# Revit family: VENTS-VK
name_source: partatom
category: Mechanical Equipment
units: mm (PartAtom-declared; Revit-internal decimal feet)

## family parameters
Always vertical = No
Classification = None
Cut with Voids When Loaded = No
OmniClass Number = 23.75.35.17.11
OmniClass Title = Fans for Air Ductwork
Part Type = Breaks Into
Room Calculation Point = No
Round Connector Dimension = Use Diameter
Shared = No
Work Plane-Based = No

## types (27) — shared parameters
Description = Inline centrifugal fan for round ducts
Family Version = 1.0
Fan Material = Plastic White Glazed
Load Classification = HVAC
Maintenance Zone Height = 600 mm
Maintenance Zone Length = 600 mm
Maintenance Zone Material = Maintenance Zone
Maintenance Zone Width = 600 mm
Manufacturer = Vents
Number of Poles = 1
Power Factor = 1
Protection rating = IPX4
R11 = 5 mm  [stored 0.0164042 ft]
R12 = 15 mm  [stored 0.0492126 ft]
R21 = 5 mm  [stored 0.0164042 ft]
R22 = 15 mm  [stored 0.0492126 ft]
URL = https://ventilation-system.com
Voltage = 230 V

## per-type parameters (varying)
- VK 100 (50Hz): Apparent Power=80 VA; BoxA=85 mm  [stored 0.278871 ft]; BoxAngle=90.00°; BoxD=250 mm  [stored 0.82021 ft]; BoxDepth=78 mm  [stored 0.255906 ft]; Current=0 A; D=100 mm  [stored 0.328084 ft]; D1=250 mm  [stored 0.82021 ft]; Duct Connection Size=100 mm  [stored 0.328084 ft]; L=230 mm  [stored 0.754593 ft]; L1=28 mm  [stored 0.0918635 ft]; L12=40 mm  [stored 0.131234 ft]; L13=40 mm  [stored 0.131234 ft]; L2=32 mm  [stored 0.104987 ft]; L22=70 mm; L23=20 mm  [stored 0.0656168 ft]; Maximum Air Flow=250 m³/h; Model=VK 100; Noise Level at 3 m (dBa)=40; Power=80 W; R1=125 mm  [stored 0.410105 ft]; RPM (min-1)=2820; Transported Air Temperature (°C)=-25...+60; Type Comments=Inline centrifugal fan VK 100; Weight=2.01 kg
- VK 100 (60Hz): Apparent Power=81 VA; BoxA=85 mm  [stored 0.278871 ft]; BoxAngle=90.00°; BoxD=250 mm  [stored 0.82021 ft]; BoxDepth=78 mm  [stored 0.255906 ft]; Current=0 A; D=100 mm  [stored 0.328084 ft]; D1=250 mm  [stored 0.82021 ft]; Duct Connection Size=100 mm  [stored 0.328084 ft]; L=230 mm  [stored 0.754593 ft]; L1=28 mm  [stored 0.0918635 ft]; L12=40 mm  [stored 0.131234 ft]; L13=40 mm  [stored 0.131234 ft]; L2=32 mm  [stored 0.104987 ft]; L22=70 mm; L23=20 mm  [stored 0.0656168 ft]; Maximum Air Flow=290 m³/h; Model=VK 100; Noise Level at 3 m (dBa)=41; Power=81 W; R1=125 mm  [stored 0.410105 ft]; RPM (min-1)=2890; Transported Air Temperature (°C)=-25...+40; Type Comments=Inline centrifugal fan VK 100; Weight=2.01 kg
- VK 125 (50Hz): Apparent Power=79 VA; BoxA=85 mm  [stored 0.278871 ft]; BoxAngle=90.00°; BoxD=250 mm  [stored 0.82021 ft]; BoxDepth=78 mm  [stored 0.255906 ft]; Current=0 A; D=125 mm  [stored 0.410105 ft]; D1=250 mm  [stored 0.82021 ft]; Duct Connection Size=125 mm  [stored 0.410105 ft]; L=220 mm  [stored 0.721785 ft]; L1=27 mm  [stored 0.0885827 ft]; L12=40 mm  [stored 0.131234 ft]; L13=40 mm  [stored 0.131234 ft]; L2=30 mm  [stored 0.0984252 ft]; L22=63 mm; L23=20 mm  [stored 0.0656168 ft]; Maximum Air Flow=355 m³/h; Model=VK 125; Noise Level at 3 m (dBa)=40; Power=79 W; R1=125 mm  [stored 0.410105 ft]; RPM (min-1)=2800; Transported Air Temperature (°C)=-25...+60; Type Comments=Inline centrifugal fan VK 125; Weight=2.20 kg
- VK 125 (60Hz): Apparent Power=81 VA; BoxA=85 mm  [stored 0.278871 ft]; BoxAngle=90.00°; BoxD=250 mm  [stored 0.82021 ft]; BoxDepth=78 mm  [stored 0.255906 ft]; Current=0 A; D=125 mm  [stored 0.410105 ft]; D1=250 mm  [stored 0.82021 ft]; Duct Connection Size=125 mm  [stored 0.410105 ft]; L=220 mm  [stored 0.721785 ft]; L1=27 mm  [stored 0.0885827 ft]; L12=40 mm  [stored 0.131234 ft]; L13=40 mm  [stored 0.131234 ft]; L2=30 mm  [stored 0.0984252 ft]; L22=63 mm; L23=20 mm  [stored 0.0656168 ft]; Maximum Air Flow=370 m³/h; Model=VK 125; Noise Level at 3 m (dBa)=41; Power=81 W; R1=125 mm  [stored 0.410105 ft]; RPM (min-1)=2830; Transported Air Temperature (°C)=-25...+40; Type Comments=Inline centrifugal fan VK 125; Weight=2.20 kg
- VK 150 (50Hz): Apparent Power=80 VA; BoxA=85 mm  [stored 0.278871 ft]; BoxAngle=90.00°; BoxD=300 mm; BoxDepth=86 mm  [stored 0.282152 ft]; Current=0 A; D=150 mm; D1=300 mm; Duct Connection Size=150 mm; L=286 mm; L1=56 mm  [stored 0.183727 ft]; L12=17 mm; L13=48 mm  [stored 0.15748 ft]; L2=64 mm  [stored 0.209974 ft]; L22=71 mm; L23=30 mm  [stored 0.0984252 ft]; Maximum Air Flow=460 m³/h; Model=VK 150; Noise Level at 3 m (dBa)=42; Power=80 W; R1=150 mm; RPM (min-1)=2725; Transported Air Temperature (°C)=-25...+60; Type Comments=Inline centrifugal fan VK 150; Weight=2.45 kg
- VK 150 (60Hz): Apparent Power=84 VA; BoxA=85 mm  [stored 0.278871 ft]; BoxAngle=90.00°; BoxD=300 mm; BoxDepth=86 mm  [stored 0.282152 ft]; Current=0 A; D=150 mm; D1=300 mm; Duct Connection Size=150 mm; L=286 mm; L1=56 mm  [stored 0.183727 ft]; L12=17 mm; L13=48 mm  [stored 0.15748 ft]; L2=64 mm  [stored 0.209974 ft]; L22=71 mm; L23=30 mm  [stored 0.0984252 ft]; Maximum Air Flow=505 m³/h; Model=VK 150; Noise Level at 3 m (dBa)=43; Power=84 W; R1=150 mm; RPM (min-1)=2840; Transported Air Temperature (°C)=-25...+40; Type Comments=Inline centrifugal fan VK 150; Weight=2.45 kg
- VK 200 (50Hz): Apparent Power=107 VA; BoxA=120 mm  [stored 0.393701 ft]; BoxAngle=60.00°; BoxD=340 mm; BoxDepth=83 mm  [stored 0.27231 ft]; Current=0 A; D=200 mm  [stored 0.656168 ft]; D1=340 mm; Duct Connection Size=200 mm  [stored 0.656168 ft]; L=276 mm  [stored 0.905512 ft]; L1=28 mm  [stored 0.0918635 ft]; L12=26 mm; L13=68 mm; L2=28 mm  [stored 0.0918635 ft]; L22=98 mm; L23=28 mm  [stored 0.0918635 ft]; Maximum Air Flow=780 m³/h; Model=VK 200; Noise Level at 3 m (dBa)=46; Power=107 W; R1=170 mm  [stored 0.557743 ft]; RPM (min-1)=2660; Transported Air Temperature (°C)=-25...+60; Type Comments=Inline centrifugal fan VK 200; Weight=3.00 kg
- VK 200 (60Hz): Apparent Power=132 VA; BoxA=120 mm  [stored 0.393701 ft]; BoxAngle=60.00°; BoxD=340 mm; BoxDepth=83 mm  [stored 0.27231 ft]; Current=1 A; D=200 mm  [stored 0.656168 ft]; D1=340 mm; Duct Connection Size=200 mm  [stored 0.656168 ft]; L=276 mm  [stored 0.905512 ft]; L1=28 mm  [stored 0.0918635 ft]; L12=26 mm; L13=68 mm; L2=28 mm  [stored 0.0918635 ft]; L22=98 mm; L23=28 mm  [stored 0.0918635 ft]; Maximum Air Flow=890 m³/h; Model=VK 200; Noise Level at 3 m (dBa)=46; Power=132 W; R1=170 mm  [stored 0.557743 ft]; RPM (min-1)=2765; Transported Air Temperature (°C)=-25...+40; Type Comments=Inline centrifugal fan VK 200; Weight=3.00 kg
- VKS 200 (50Hz): Apparent Power=173 VA; BoxA=120 mm  [stored 0.393701 ft]; BoxAngle=60.00°; BoxD=366 mm; BoxDepth=83 mm  [stored 0.27231 ft]; Current=1 A; D=200 mm  [stored 0.656168 ft]; D1=340 mm; Duct Connection Size=200 mm  [stored 0.656168 ft]; L=276 mm  [stored 0.905512 ft]; L1=28 mm  [stored 0.0918635 ft]; L12=26 mm; L13=68 mm; L2=28 mm  [stored 0.0918635 ft]; L22=98 mm; L23=28 mm  [stored 0.0918635 ft]; Maximum Air Flow=930 m³/h; Model=VKS 200; Noise Level at 3 m (dBa)=48; Power=173 W; R1=170 mm  [stored 0.557743 ft]; RPM (min-1)=2425; Transported Air Temperature (°C)=-25...+60; Type Comments=Inline centrifugal fan VKS 200; Weight=4.30 kg
- VKS 200 (60Hz): Apparent Power=216 VA; BoxA=120 mm  [stored 0.393701 ft]; BoxAngle=60.00°; BoxD=366 mm; BoxDepth=83 mm  [stored 0.27231 ft]; Current=1 A; D=200 mm  [stored 0.656168 ft]; D1=340 mm; Duct Connection Size=200 mm  [stored 0.656168 ft]; L=276 mm  [stored 0.905512 ft]; L1=28 mm  [stored 0.0918635 ft]; L12=26 mm; L13=68 mm; L2=28 mm  [stored 0.0918635 ft]; L22=98 mm; L23=28 mm  [stored 0.0918635 ft]; Maximum Air Flow=1020 m³/h; Model=VKS 200; Noise Level at 3 m (dBa)=49; Power=216 W; R1=170 mm  [stored 0.557743 ft]; RPM (min-1)=2155; Transported Air Temperature (°C)=-25...+40; Type Comments=Inline centrifugal fan VKS 200; Weight=4.30 kg
- VK 250 (50Hz): Apparent Power=173 VA; BoxA=120 mm  [stored 0.393701 ft]; BoxAngle=60.00°; BoxD=340 mm; BoxDepth=83 mm  [stored 0.27231 ft]; Current=1 A; D=250 mm  [stored 0.82021 ft]; D1=340 mm; Duct Connection Size=250 mm  [stored 0.82021 ft]; L=265 mm  [stored 0.869423 ft]; L1=25 mm  [stored 0.082021 ft]; L12=27 mm  [stored 0.0885827 ft]; L13=56 mm  [stored 0.183727 ft]; L2=65 mm  [stored 0.213255 ft]; L22=64 mm  [stored 0.209974 ft]; L23=28 mm  [stored 0.0918635 ft]; Maximum Air Flow=1080 m³/h; Model=VK 250; Noise Level at 3 m (dBa)=49; Power=173 W; R1=170 mm  [stored 0.557743 ft]; RPM (min-1)=2090; Transported Air Temperature (°C)=-25...+60; Type Comments=Inline centrifugal fan VK 250; Weight=4.30 kg
- VK 250 (60Hz): Apparent Power=207 VA; BoxA=120 mm  [stored 0.393701 ft]; BoxAngle=60.00°; BoxD=340 mm; BoxDepth=83 mm  [stored 0.27231 ft]; Current=1 A; D=250 mm  [stored 0.82021 ft]; D1=340 mm; Duct Connection Size=250 mm  [stored 0.82021 ft]; L=265 mm  [stored 0.869423 ft]; L1=25 mm  [stored 0.082021 ft]; L12=27 mm  [stored 0.0885827 ft]; L13=56 mm  [stored 0.183727 ft]; L2=65 mm  [stored 0.213255 ft]; L22=64 mm  [stored 0.209974 ft]; L23=28 mm  [stored 0.0918635 ft]; Maximum Air Flow=1090 m³/h; Model=VK 250; Noise Level at 3 m (dBa)=50; Power=207 W; R1=170 mm  [stored 0.557743 ft]; RPM (min-1)=2120; Transported Air Temperature (°C)=-25...+40; Type Comments=Inline centrifugal fan VK 250; Weight=4.30 kg
- VK 315 (50Hz): Apparent Power=200 VA; BoxA=120 mm  [stored 0.393701 ft]; BoxAngle=120.00°; BoxD=432 mm; BoxDepth=85 mm  [stored 0.278871 ft]; Current=1 A; D=315 mm; D1=400 mm; Duct Connection Size=315 mm; L=276 mm  [stored 0.905512 ft]; L1=55 mm  [stored 0.180446 ft]; L12=25 mm  [stored 0.082021 ft]; L13=62 mm  [stored 0.203412 ft]; L2=40 mm  [stored 0.131234 ft]; L22=63 mm; L23=31 mm  [stored 0.101706 ft]; Maximum Air Flow=1340 m³/h; Model=VK 315; Noise Level at 3 m (dBa)=48; Power=200 W; R1=200 mm  [stored 0.656168 ft]; RPM (min-1)=2655; Transported Air Temperature (°C)=-25...+60; Type Comments=Inline centrifugal fan VK 315; Weight=4.85 kg
- VK 315 (60Hz): Apparent Power=213 VA; BoxA=120 mm  [stored 0.393701 ft]; BoxAngle=120.00°; BoxD=432 mm; BoxDepth=85 mm  [stored 0.278871 ft]; Current=1 A; D=315 mm; D1=400 mm; Duct Connection Size=315 mm; L=276 mm  [stored 0.905512 ft]; L1=55 mm  [stored 0.180446 ft]; L12=25 mm  [stored 0.082021 ft]; L13=62 mm  [stored 0.203412 ft]; L2=40 mm  [stored 0.131234 ft]; L22=63 mm; L23=31 mm  [stored 0.101706 ft]; Maximum Air Flow=1290 m³/h; Model=VK 315; Noise Level at 3 m (dBa)=48; Power=213 W; R1=200 mm  [stored 0.656168 ft]; RPM (min-1)=2590; Transported Air Temperature (°C)=-25...+40; Type Comments=Inline centrifugal fan VK 315; Weight=4.85 kg
- VKS 315 (50Hz): Apparent Power=310 VA; BoxA=120 mm  [stored 0.393701 ft]; BoxAngle=120.00°; BoxD=424 mm; BoxDepth=85 mm  [stored 0.278871 ft]; Current=1 A; D=315 mm; D1=400 mm; Duct Connection Size=315 mm; L=276 mm  [stored 0.905512 ft]; L1=55 mm  [stored 0.180446 ft]; L12=25 mm  [stored 0.082021 ft]; L13=62 mm  [stored 0.203412 ft]; L2=40 mm  [stored 0.131234 ft]; L22=63 mm; L23=31 mm  [stored 0.101706 ft]; Maximum Air Flow=1700 m³/h; Model=VKS 315; Noise Level at 3 m (dBa)=57; Power=310 W; R1=200 mm  [stored 0.656168 ft]; RPM (min-1)=2590; Transported Air Temperature (°C)=-25...+60; Type Comments=Inline centrifugal fan VKS 315; Weight=4.85 kg
- VK 100 Duo (min): Apparent Power=45 VA; BoxA=85 mm  [stored 0.278871 ft]; BoxAngle=90.00°; BoxD=250 mm  [stored 0.82021 ft]; BoxDepth=78 mm  [stored 0.255906 ft]; Current=0 A; D=100 mm  [stored 0.328084 ft]; D1=250 mm  [stored 0.82021 ft]; Duct Connection Size=100 mm  [stored 0.328084 ft]; L=230 mm  [stored 0.754593 ft]; L1=27 mm  [stored 0.0885827 ft]; L12=40 mm  [stored 0.131234 ft]; L13=40 mm  [stored 0.131234 ft]; L2=30 mm  [stored 0.0984252 ft]; L22=73 mm; L23=20 mm  [stored 0.0656168 ft]; Maximum Air Flow=157 m³/h; Model=VK 100 Duo; Noise Level at 3 m (dBa)=38; Power=45 W; R1=125 mm  [stored 0.410105 ft]; RPM (min-1)=1820; Transported Air Temperature (°C)=-25...+60; Type Comments=Inline centrifugal fan VK 100 Duo; Weight=2.01 kg
- VK 100 Duo (max): Apparent Power=57 VA; BoxA=85 mm  [stored 0.278871 ft]; BoxAngle=90.00°; BoxD=250 mm  [stored 0.82021 ft]; BoxDepth=78 mm  [stored 0.255906 ft]; Current=0 A; D=100 mm  [stored 0.328084 ft]; D1=250 mm  [stored 0.82021 ft]; Duct Connection Size=100 mm  [stored 0.328084 ft]; L=230 mm  [stored 0.754593 ft]; L1=27 mm  [stored 0.0885827 ft]; L12=40 mm  [stored 0.131234 ft]; L13=40 mm  [stored 0.131234 ft]; L2=30 mm  [stored 0.0984252 ft]; L22=73 mm; L23=20 mm  [stored 0.0656168 ft]; Maximum Air Flow=264 m³/h; Model=VK 100 Duo; Noise Level at 3 m (dBa)=38; Power=57 W; R1=125 mm  [stored 0.410105 ft]; RPM (min-1)=2440; Transported Air Temperature (°C)=-25...+60; Type Comments=Inline centrifugal fan VK 100 Duo; Weight=2.01 kg
- VK 125 Duo (min): Apparent Power=45 VA; BoxA=85 mm  [stored 0.278871 ft]; BoxAngle=90.00°; BoxD=250 mm  [stored 0.82021 ft]; BoxDepth=78 mm  [stored 0.255906 ft]; Current=0 A; D=125 mm  [stored 0.410105 ft]; D1=250 mm  [stored 0.82021 ft]; Duct Connection Size=125 mm  [stored 0.410105 ft]; L=220 mm  [stored 0.721785 ft]; L1=27 mm  [stored 0.0885827 ft]; L12=40 mm  [stored 0.131234 ft]; L13=40 mm  [stored 0.131234 ft]; L2=30 mm  [stored 0.0984252 ft]; L22=63 mm; L23=20 mm  [stored 0.0656168 ft]; Maximum Air Flow=191 m³/h; Model=VK 125 Duo; Noise Level at 3 m (dBa)=39; Power=45 W; R1=125 mm  [stored 0.410105 ft]; RPM (min-1)=1810; Transported Air Temperature (°C)=-25...+60; Type Comments=Inline centrifugal fan VK 125 Duo; Weight=2.20 kg
- VK 125 Duo (max): Apparent Power=58 VA; BoxA=85 mm  [stored 0.278871 ft]; BoxAngle=90.00°; BoxD=250 mm  [stored 0.82021 ft]; BoxDepth=78 mm  [stored 0.255906 ft]; Current=0 A; D=125 mm  [stored 0.410105 ft]; D1=250 mm  [stored 0.82021 ft]; Duct Connection Size=125 mm  [stored 0.410105 ft]; L=220 mm  [stored 0.721785 ft]; L1=27 mm  [stored 0.0885827 ft]; L12=40 mm  [stored 0.131234 ft]; L13=40 mm  [stored 0.131234 ft]; L2=30 mm  [stored 0.0984252 ft]; L22=63 mm; L23=20 mm  [stored 0.0656168 ft]; Maximum Air Flow=329 m³/h; Model=VK 125 Duo; Noise Level at 3 m (dBa)=39; Power=58 W; R1=125 mm  [stored 0.410105 ft]; RPM (min-1)=2380; Transported Air Temperature (°C)=-25...+60; Type Comments=Inline centrifugal fan VK 125 Duo; Weight=2.20 kg
- VK 150 Duo (min): Apparent Power=46 VA; BoxA=85 mm  [stored 0.278871 ft]; BoxAngle=90.00°; BoxD=300 mm; BoxDepth=86 mm  [stored 0.282152 ft]; Current=0 A; D=150 mm; D1=300 mm; Duct Connection Size=150 mm; L=286 mm; L1=56 mm  [stored 0.183727 ft]; L12=17 mm; L13=48 mm  [stored 0.15748 ft]; L2=64 mm  [stored 0.209974 ft]; L22=71 mm; L23=30 mm  [stored 0.0984252 ft]; Maximum Air Flow=264 m³/h; Model=VK 150 Duo; Noise Level at 3 m (dBa)=40; Power=46 W; R1=150 mm; RPM (min-1)=1805; Transported Air Temperature (°C)=-25...+60; Type Comments=Inline centrifugal fan VK 150 Duo; Weight=2.45 kg
- VK 150 Duo (max): Apparent Power=59 VA; BoxA=85 mm  [stored 0.278871 ft]; BoxAngle=90.00°; BoxD=300 mm; BoxDepth=86 mm  [stored 0.282152 ft]; Current=0 A; D=150 mm; D1=300 mm; Duct Connection Size=150 mm; L=286 mm; L1=56 mm  [stored 0.183727 ft]; L12=17 mm; L13=48 mm  [stored 0.15748 ft]; L2=64 mm  [stored 0.209974 ft]; L22=71 mm; L23=30 mm  [stored 0.0984252 ft]; Maximum Air Flow=445 m³/h; Model=VK 150 Duo; Noise Level at 3 m (dBa)=40; Power=59 W; R1=150 mm; RPM (min-1)=2420; Transported Air Temperature (°C)=-25...+60; Type Comments=Inline centrifugal fan VK 150 Duo; Weight=2.45 kg
- VK 200 Duo (min): Apparent Power=83 VA; BoxA=120 mm  [stored 0.393701 ft]; BoxAngle=60.00°; BoxD=340 mm; BoxDepth=83 mm  [stored 0.27231 ft]; Current=0 A; D=200 mm  [stored 0.656168 ft]; D1=340 mm; Duct Connection Size=200 mm  [stored 0.656168 ft]; L=276 mm  [stored 0.905512 ft]; L1=28 mm  [stored 0.0918635 ft]; L12=26 mm; L13=68 mm; L2=28 mm  [stored 0.0918635 ft]; L22=98 mm; L23=28 mm  [stored 0.0918635 ft]; Maximum Air Flow=430 m³/h; Model=VK 200 Duo; Noise Level at 3 m (dBa)=42; Power=83 W; R1=170 mm  [stored 0.557743 ft]; RPM (min-1)=1920; Transported Air Temperature (°C)=-25...+60; Type Comments=Inline centrifugal fan VK 200 Duo; Weight=3.00 kg
- VK 200 Duo (max): Apparent Power=95 VA; BoxA=120 mm  [stored 0.393701 ft]; BoxAngle=60.00°; BoxD=340 mm; BoxDepth=83 mm  [stored 0.27231 ft]; Current=0 A; D=200 mm  [stored 0.656168 ft]; D1=340 mm; Duct Connection Size=200 mm  [stored 0.656168 ft]; L=276 mm  [stored 0.905512 ft]; L1=28 mm  [stored 0.0918635 ft]; L12=26 mm; L13=68 mm; L2=28 mm  [stored 0.0918635 ft]; L22=98 mm; L23=28 mm  [stored 0.0918635 ft]; Maximum Air Flow=741 m³/h; Model=VK 200 Duo; Noise Level at 3 m (dBa)=42; Power=95 W; R1=170 mm  [stored 0.557743 ft]; RPM (min-1)=2470; Transported Air Temperature (°C)=-25...+60; Type Comments=Inline centrifugal fan VK 200 Duo; Weight=3.00 kg
- VK 250 Duo (min): Apparent Power=147 VA; BoxA=120 mm  [stored 0.393701 ft]; BoxAngle=60.00°; BoxD=340 mm; BoxDepth=83 mm  [stored 0.27231 ft]; Current=1 A; D=250 mm  [stored 0.82021 ft]; D1=340 mm; Duct Connection Size=250 mm  [stored 0.82021 ft]; L=265 mm  [stored 0.869423 ft]; L1=25 mm  [stored 0.082021 ft]; L12=27 mm  [stored 0.0885827 ft]; L13=56 mm  [stored 0.183727 ft]; L2=65 mm  [stored 0.213255 ft]; L22=64 mm  [stored 0.209974 ft]; L23=28 mm  [stored 0.0918635 ft]; Maximum Air Flow=642 m³/h; Model=VK 250 Duo; Noise Level at 3 m (dBa)=46; Power=147 W; R1=170 mm  [stored 0.557743 ft]; RPM (min-1)=1940; Transported Air Temperature (°C)=-25...+60; Type Comments=Inline centrifugal fan VK 250 Duo; Weight=4.30 kg
- VK 250 Duo (max): Apparent Power=176 VA; BoxA=120 mm  [stored 0.393701 ft]; BoxAngle=60.00°; BoxD=340 mm; BoxDepth=83 mm  [stored 0.27231 ft]; Current=1 A; D=250 mm  [stored 0.82021 ft]; D1=340 mm; Duct Connection Size=250 mm  [stored 0.82021 ft]; L=265 mm  [stored 0.869423 ft]; L1=25 mm  [stored 0.082021 ft]; L12=27 mm  [stored 0.0885827 ft]; L13=56 mm  [stored 0.183727 ft]; L2=65 mm  [stored 0.213255 ft]; L22=64 mm  [stored 0.209974 ft]; L23=28 mm  [stored 0.0918635 ft]; Maximum Air Flow=1126 m³/h; Model=VK 250 Duo; Noise Level at 3 m (dBa)=46; Power=176 W; R1=170 mm  [stored 0.557743 ft]; RPM (min-1)=2370; Transported Air Temperature (°C)=-25...+60; Type Comments=Inline centrifugal fan VK 250 Duo; Weight=4.30 kg
- VK 315 Duo (min): Apparent Power=143 VA; BoxA=120 mm  [stored 0.393701 ft]; BoxAngle=120.00°; BoxD=400 mm; BoxDepth=85 mm  [stored 0.278871 ft]; Current=1 A; D=315 mm; D1=400 mm; Duct Connection Size=315 mm; L=276 mm  [stored 0.905512 ft]; L1=55 mm  [stored 0.180446 ft]; L12=25 mm  [stored 0.082021 ft]; L13=62 mm  [stored 0.203412 ft]; L2=40 mm  [stored 0.131234 ft]; L22=63 mm; L23=31 mm  [stored 0.101706 ft]; Maximum Air Flow=758 m³/h; Model=VK 315 Duo; Noise Level at 3 m (dBa)=48; Power=143 W; R1=200 mm  [stored 0.656168 ft]; RPM (min-1)=1870; Transported Air Temperature (°C)=-25...+60; Type Comments=Inline centrifugal fan VK 315 Duo; Weight=4.85 kg
- VK 315 Duo (max): Apparent Power=173 VA; BoxA=120 mm  [stored 0.393701 ft]; BoxAngle=120.00°; BoxD=400 mm; BoxDepth=85 mm  [stored 0.278871 ft]; Current=1 A; D=315 mm; D1=400 mm; Duct Connection Size=315 mm; L=276 mm  [stored 0.905512 ft]; L1=55 mm  [stored 0.180446 ft]; L12=25 mm  [stored 0.082021 ft]; L13=62 mm  [stored 0.203412 ft]; L2=40 mm  [stored 0.131234 ft]; L22=63 mm; L23=31 mm  [stored 0.101706 ft]; Maximum Air Flow=1268 m³/h; Model=VK 315 Duo; Noise Level at 3 m (dBa)=48; Power=173 W; R1=200 mm  [stored 0.656168 ft]; RPM (min-1)=2410; Transported Air Temperature (°C)=-25...+60; Type Comments=Inline centrifugal fan VK 315 Duo; Weight=4.85 kg

note: [stored X ft] marks values corroborated as IEEE doubles in the binary element streams (Revit-internal decimal feet)

## geometry (parser evidence)
native form markers: Sweep x8
no freeform markers — native parametric forms only
